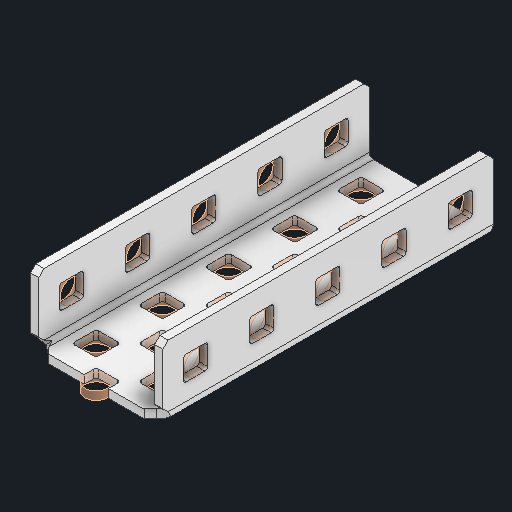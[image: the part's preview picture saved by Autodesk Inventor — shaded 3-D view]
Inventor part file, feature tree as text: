
AUTODESK INVENTOR PART (.ipt)
format: ipt  version: 2024 (Build 280153000, 153)  size: 572,416 bytes
history: native  units: in
note: dims shown in document units (in); Inventor stores cm internally (conversion verified against a paired STEP export)
features: other x56, sketch x5, sheet_metal_op x1
ambient origin geometry x8: Origin, YZ Plane, XZ Plane, XY Plane, X Axis, Y Axis, Z Axis, Center Point
bodies: Solid1 (feature_tree)
feature tree (62):
  other  "Alu C 1x2x1x5.ipt"
  other  "Solid1::Alu C 1x2x1x5.ipt"
  other  "TaggingFeature1"
  sketch  "Sketch1"  dims[d0=0.3937in]
  sketch  "Sketch2"  dims[d1=0.0625in]
  sketch  "Sketch3"
  other  "Flange Pattern Sketch"
  sketch  "Sketch9"
  sheet_metal_op  "Body Pattern Sketch"
  other  "Arc Length"
  sketch  "Sketch14"
  other  "Flange Pattern Plane"
  other  "Srf1"
  other  "Srf2"
  other  "Srf3"
  other  "Srf4"
  other  "Srf5"
  other  "Srf6"
  other  "Srf7"
  other  "Srf8"
  other  "Srf9"
  other  "Srf10"
  other  "Srf11"
  other  "Srf12"
  other  "Srf13"
  other  "Srf14"
  other  "Srf15"
  other  "Srf16"
  other  "Srf17"
  other  "Srf18"
  other  "Srf19"
  other  "Srf20"
  other  "Srf21"
  other  "Srf22"
  other  "Srf23"
  other  "Srf24"
  other  "Srf25"
  other  "Srf1::Derived"
  other  "Srf2::Derived"
  other  "Srf823::Derived"
  other  "Srf824::Derived"
  other  "Srf825::Derived"
  other  "Srf826::Derived"
  other  "Srf827::Derived"
  other  "Srf828::Derived"
  other  "Srf829::Derived"
  other  "Srf922::Derived"
  other  "Srf91::Derived"
  other  "Srf92::Derived"
  other  "Srf856::Derived"
  other  "Srf857::Derived"
  other  "Srf858::Derived"
  other  "Srf859::Derived"
  other  "Srf860::Derived"
  other  "Srf861::Derived"
  other  "Srf862::Derived"
  other  "Srf959::Derived"
  other  "Srf786::Derived"
  other  "Srf889::Derived"
  other  "Srf890::Derived"
  other  "Srf891::Derived"
  other  "Srf892::Derived"
